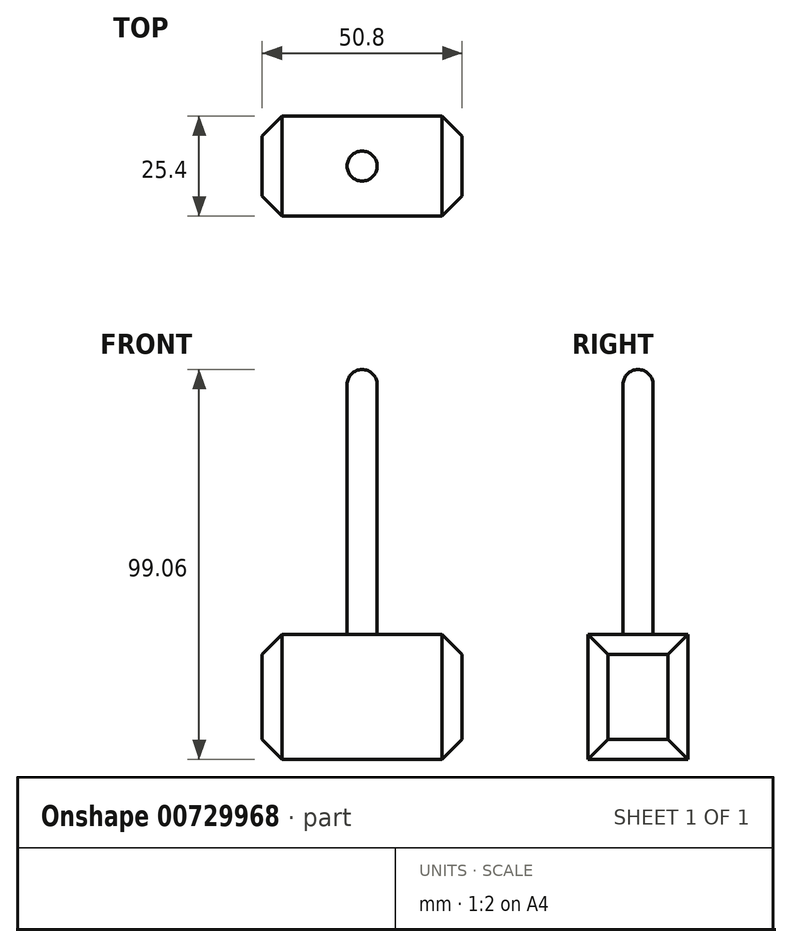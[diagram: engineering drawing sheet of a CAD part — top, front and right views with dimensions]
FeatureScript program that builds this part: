
annotation { "Feature Type Name" : "Feature", "Feature Type Description" : "" }
export const myFeature = defineFeature(function(context is Context, id is Id, definition is map)
    precondition{}
    {
        {
            var Q0;
            Q0=qCreatedBy(makeId("Top.planeOp"),FACE);
            var sketch = newSketch(context, id + "F0", { "sketchPlane" : qUnion([Q0])});
            skLineSegment(sketch, "E0.bottom", {"start": v(-25.4, 12.7) * mm, "end": v(25.4, 12.7) * mm});
            skLineSegment(sketch, "E0.top", {"start": v(-25.4, -12.7) * mm, "end": v(25.4, -12.7) * mm});
            skLineSegment(sketch, "E0.left", {"start": v(-25.4, 12.7) * mm, "end": v(-25.4, -12.7) * mm});
            skLineSegment(sketch, "E0.right", {"start": v(25.4, 12.7) * mm, "end": v(25.4, -12.7) * mm});
            skPoint(sketch, "E0.middle", {"position": v(0, 0) * mm});
            skSolve(sketch);
        }
        {
            var Q0;
            Q0=makeQuery(id+"F0.imprint","IMPRINT",FACE,{"disambiguationData":[TD([[makeQuery(id+"F0.imprint","IMPRINT",EDGE,{"derivedFrom":sQuery(id+"F0.wireOp",EDGE,"E0.bottom")}),-1.0]])]});
            extrude(context, id + "F1", {"entities" : qUnion([Q0]), "depth" : 31.75 * mm, "offsetDistance" : 25.4 * mm});
        }
        {
            var Q0;
            Q0=makeQuery(id+"F1.opExtrude","CAP_FACE",FACE,{"disambiguationData":[OSD([sQuery(id+"F0.wireOp",EDGE,"E0.bottom"),sQuery(id+"F0.wireOp",EDGE,"E0.top"),sQuery(id+"F0.wireOp",EDGE,"E0.left"),sQuery(id+"F0.wireOp",EDGE,"E0.right")])],"isStart":false});
            var sketch = newSketch(context, id + "F2", { "sketchPlane" : qUnion([Q0])});
            skCircle(sketch, "E1", {"center": v(0, 0) * mm, "radius": 3.81 * mm});
            skSolve(sketch);
        }
        {
            var Q0;
            Q0=makeQuery(id+"F2.imprint","IMPRINT",FACE,{"disambiguationData":[TD([[makeQuery(id+"F2.imprint","IMPRINT",EDGE,{"derivedFrom":sQuery(id+"F2.wireOp",EDGE,"E1")}),1.0]])]});
            extrude(context, id + "F3", {"entities" : qUnion([Q0]), "operationType" : NewBodyOperationType.ADD, "depth" : 63.5 * mm, "offsetDistance" : 25.4 * mm});
        }
        {
            var Q0;
            Q0=makeQuery(id+"F3.opExtrude","CAP_FACE",FACE,{"disambiguationData":[OSD([sQuery(id+"F2.wireOp",EDGE,"E1")])],"isStart":false});
            var sketch = newSketch(context, id + "F4", { "sketchPlane" : qUnion([Q0])});
            skArc(sketch, "E2", {"start": v(0, -3.81) * mm, "mid": v(3.83, 0) * mm, "end": v(0, 3.81) * mm});
            skLineSegment(sketch, "E3", {"start": v(0, 3.81) * mm, "end": v(0, -3.81) * mm});
            skSolve(sketch);
        }
        {
            var Q0;
            {var subQ0=sQuery(id+"F4.wireOp",EDGE,"E3");Q0=makeQuery(id+"F4.imprint","IMPRINT",FACE,{"disambiguationData":[TD([[makeQuery(id+"F4.imprint","IMPRINT",EDGE,{"derivedFrom":subQ0}),1.0]])]});}
            var Q1;
            Q1=sQuery(id+"F4.wireOp",EDGE,"E3");
            revolve(context, id + "F5", {"operationType" : NewBodyOperationType.ADD, "surfaceOperationType" : NewSurfaceOperationType.NEW, "entities" : qUnion([Q0]), "axis" : qUnion([Q1]), "revolveType" : RevolveType.FULL});
        }
        {
            var Q0;
            Q0=makeQuery(id+"F1.opExtrude","CAP_EDGE",EDGE,{"disambiguationData":[OSD([sQuery(id+"F0.wireOp",EDGE,"E0.right")])],"isStart":true});
            var Q1;
            Q1=makeQuery(id+"F1.opExtrude","SWEPT_EDGE",EDGE,{"disambiguationData":[OSD([sQuery(id+"F0.wireOp",EDGE,"E0.bottom"),sQuery(id+"F0.wireOp",EDGE,"E0.right")])]});
            var Q2;
            Q2=makeQuery(id+"F1.opExtrude","CAP_EDGE",EDGE,{"disambiguationData":[OSD([sQuery(id+"F0.wireOp",EDGE,"E0.right")])],"isStart":false});
            var Q3;
            Q3=makeQuery(id+"F1.opExtrude","SWEPT_EDGE",EDGE,{"disambiguationData":[OSD([sQuery(id+"F0.wireOp",EDGE,"E0.top"),sQuery(id+"F0.wireOp",EDGE,"E0.right")])]});
            chamfer(context, id + "F6", {"entities" : qUnion([Q0, Q1, Q2, Q3]), "width" : 5.08 * mm, "tangentPropagation" : true});
        }
        {
            var Q0;
            Q0=makeQuery(id+"F1.opExtrude","CAP_EDGE",EDGE,{"disambiguationData":[OSD([sQuery(id+"F0.wireOp",EDGE,"E0.left")])],"isStart":false});
            var Q1;
            Q1=makeQuery(id+"F1.opExtrude","SWEPT_EDGE",EDGE,{"disambiguationData":[OSD([sQuery(id+"F0.wireOp",EDGE,"E0.bottom"),sQuery(id+"F0.wireOp",EDGE,"E0.left")])]});
            var Q2;
            Q2=makeQuery(id+"F1.opExtrude","SWEPT_FACE",FACE,{"disambiguationData":[OSD([sQuery(id+"F0.wireOp",EDGE,"E0.left")])]});
            chamfer(context, id + "F7", {"entities" : qUnion([Q0, Q1, Q2]), "width" : 5.08 * mm, "tangentPropagation" : true});
        }
    });
